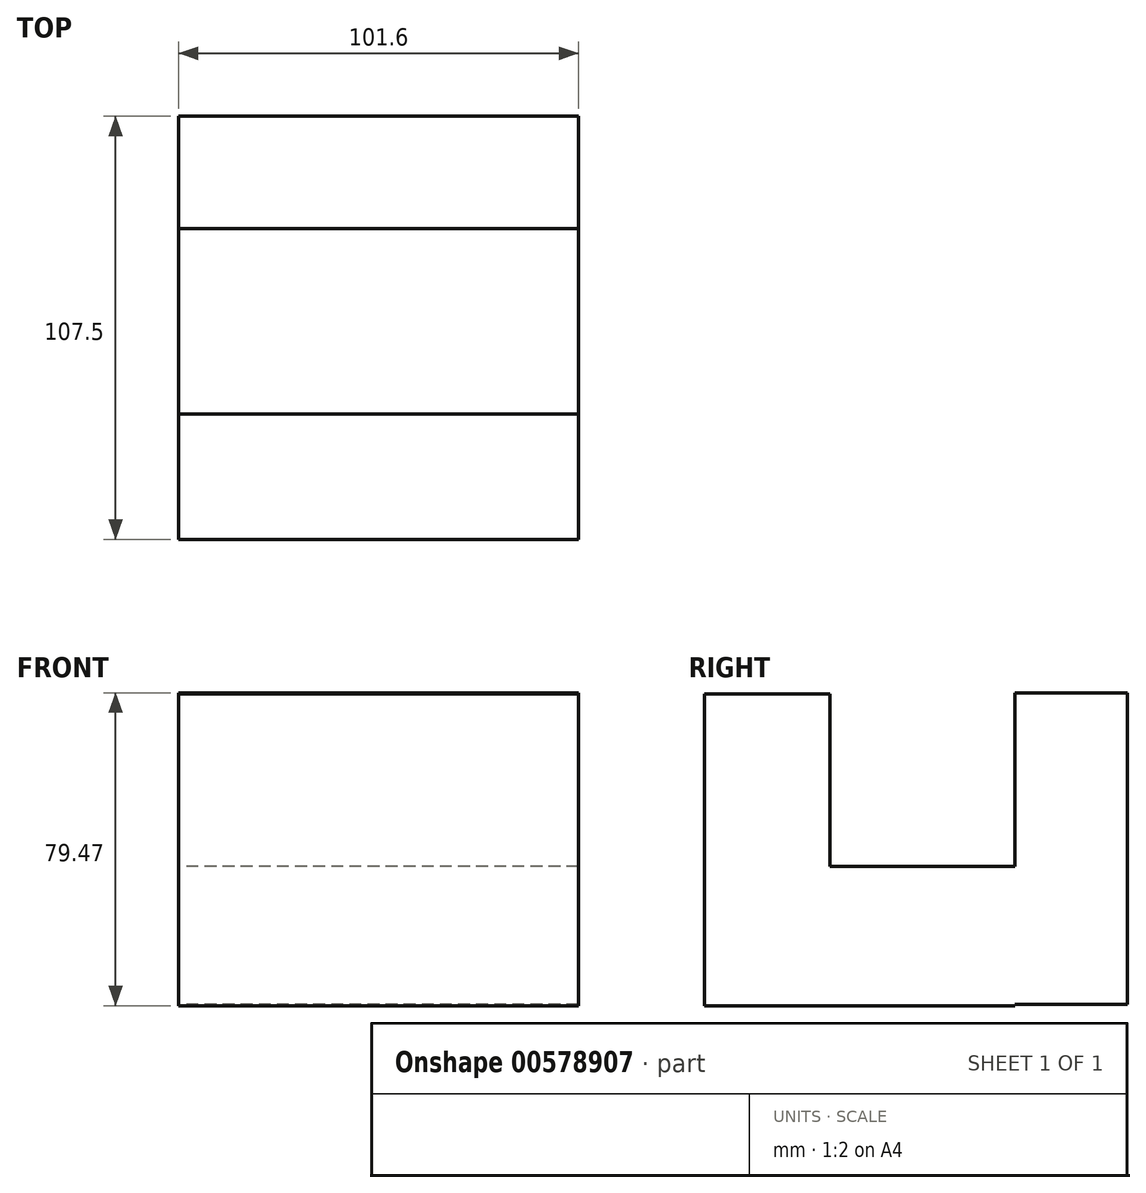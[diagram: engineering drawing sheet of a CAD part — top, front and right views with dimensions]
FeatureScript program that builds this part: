
annotation { "Feature Type Name" : "Feature", "Feature Type Description" : "" }
export const myFeature = defineFeature(function(context is Context, id is Id, definition is map)
    precondition{}
    {
        {
            var Q0;
            Q0=qCreatedBy(makeId("Right.planeOp"),FACE);
            var sketch = newSketch(context, id + "F0", { "sketchPlane" : qUnion([Q0])});
            skLineSegment(sketch, "E0.bottom", {"start": v(55.52, 44.09) * mm, "end": v(26.94, 44.09) * mm});
            skLineSegment(sketch, "E0.top", {"start": v(55.52, -35.1) * mm, "end": v(26.94, -35.1) * mm});
            skLineSegment(sketch, "E0.left", {"start": v(55.52, 44.09) * mm, "end": v(55.52, -35.1) * mm});
            skLineSegment(sketch, "E0.right", {"start": v(26.94, 44.09) * mm, "end": v(26.94, -35.1) * mm});
            skLineSegment(sketch, "E1.bottom", {"start": v(26.94, 0) * mm, "end": v(-20.14, 0) * mm});
            skLineSegment(sketch, "E1.top", {"start": v(26.94, -35.38) * mm, "end": v(-20.14, -35.38) * mm});
            skLineSegment(sketch, "E1.left", {"start": v(26.94, 0) * mm, "end": v(26.94, -35.38) * mm});
            skLineSegment(sketch, "E1.right", {"start": v(-20.14, 0) * mm, "end": v(-20.14, -35.38) * mm});
            skLineSegment(sketch, "E2.bottom", {"start": v(-20.14, -35.38) * mm, "end": v(-51.98, -35.38) * mm});
            skLineSegment(sketch, "E2.top", {"start": v(-20.14, 43.82) * mm, "end": v(-51.98, 43.82) * mm});
            skLineSegment(sketch, "E2.left", {"start": v(-20.14, -35.38) * mm, "end": v(-20.14, 43.82) * mm});
            skLineSegment(sketch, "E2.right", {"start": v(-51.98, -35.38) * mm, "end": v(-51.98, 43.82) * mm});
            skSolve(sketch);
        }
        {
            var Q0;
            Q0 = qSketchRegion(id + "F0", true);
            extrude(context, id + "F1", {"entities" : qUnion([Q0]), "depth" : 101.6 * mm, "offsetDistance" : 25.4 * mm});
        }
    });
